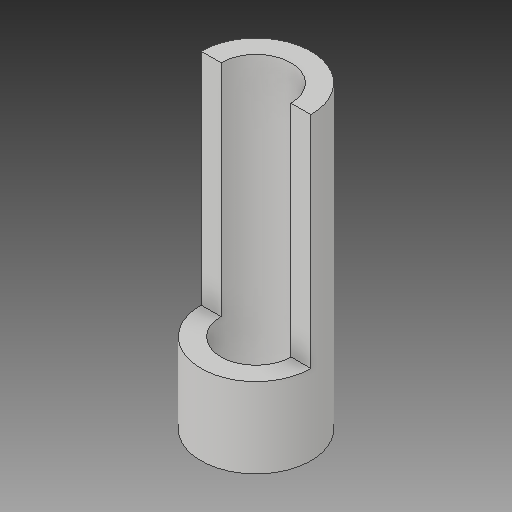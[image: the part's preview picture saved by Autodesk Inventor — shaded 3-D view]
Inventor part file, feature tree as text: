
AUTODESK INVENTOR PART (.ipt)
format: ipt  version: 2018 (Build 220112000, 112)  size: 115,200 bytes
history: native  units: mm
features: extrude x2, sketch x2, projected_geometry x1
ambient origin geometry x8: Origin, YZ Plane, XZ Plane, XY Plane, X Axis, Y Axis, Z Axis, Center Point
bodies: Solid1 (feature_tree)
feature tree (5):
  extrude  "Extrusion1"  Depth=5.5mm
  extrude  "Extrusion2"  Depth=11.0mm TaperAngle=0.0deg
  sketch  "Sketch1"  dims[d0=3.5mm d1=5.5mm]
  sketch  "Sketch2"  dims[d2=4.0mm d3=0.0mm d4=11.0mm d5=0.0mm]
  projected_geometry  "Projected Loop1"
